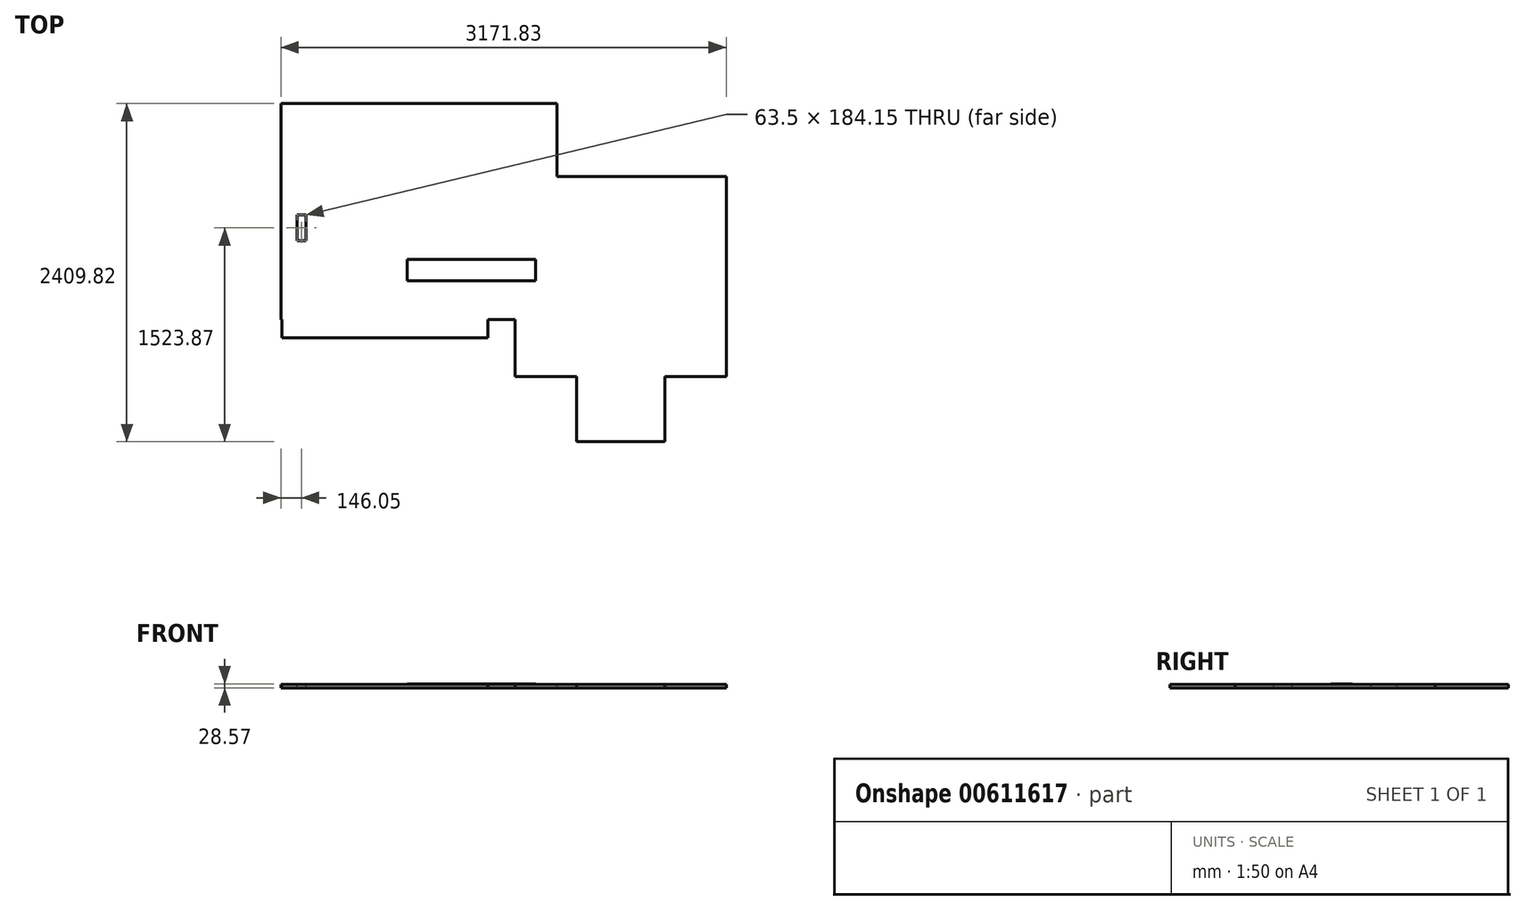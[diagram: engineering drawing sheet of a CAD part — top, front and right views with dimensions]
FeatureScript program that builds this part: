
annotation { "Feature Type Name" : "Feature", "Feature Type Description" : "" }
export const myFeature = defineFeature(function(context is Context, id is Id, definition is map)
    precondition{}
    {
        {
            var Q0;
            Q0=qCreatedBy(makeId("Top.planeOp"),FACE);
            var sketch = newSketch(context, id + "F0", { "sketchPlane" : qUnion([Q0])});
            skLineSegment(sketch, "E0", {"start": v(-1397, 266.7) * mm, "end": v(-1397, -1273.3) * mm});
            skLineSegment(sketch, "E1", {"start": v(-1397, 266.7) * mm, "end": v(568.33, 266.7) * mm});
            skLineSegment(sketch, "E2", {"start": v(1774.83, -254) * mm, "end": v(1774.83, -1679.58) * mm});
            skLineSegment(sketch, "E3", {"start": v(708.15, -2143.12) * mm, "end": v(1336.67, -2143.12) * mm});
            skLineSegment(sketch, "E4", {"start": v(1774.83, -254) * mm, "end": v(568.33, -254) * mm});
            skLineSegment(sketch, "E5", {"start": v(568.33, -254) * mm, "end": v(568.33, 266.7) * mm});
            skLineSegment(sketch, "E6", {"start": v(-1390.65, -1403.48) * mm, "end": v(76.2, -1403.48) * mm});
            skLineSegment(sketch, "E7", {"start": v(76.2, -1403.48) * mm, "end": v(76.2, -1273.17) * mm});
            skLineSegment(sketch, "E8", {"start": v(76.2, -1273.17) * mm, "end": v(270, -1273.17) * mm});
            skLineSegment(sketch, "E9", {"start": v(270, -1273.17) * mm, "end": v(270, -1679.57) * mm});
            skLineSegment(sketch, "E10", {"start": v(270, -1679.57) * mm, "end": v(708.15, -1679.57) * mm});
            skLineSegment(sketch, "E11", {"start": v(708.15, -1679.57) * mm, "end": v(708.15, -2143.12) * mm});
            skLineSegment(sketch, "E12", {"start": v(1774.83, -1679.57) * mm, "end": v(1336.67, -1679.57) * mm});
            skLineSegment(sketch, "E13", {"start": v(1336.67, -1679.57) * mm, "end": v(1336.67, -2143.12) * mm});
            skLineSegment(sketch, "E14", {"start": v(-1397, -1273.3) * mm, "end": v(-1390.65, -1273.3) * mm});
            skLineSegment(sketch, "E15", {"start": v(-1390.65, -1273.3) * mm, "end": v(-1390.65, -1403.48) * mm});
            skLineSegment(sketch, "E16", {"start": v(-1282.7, -711.33) * mm, "end": v(-1219.2, -711.33) * mm});
            skLineSegment(sketch, "E17", {"start": v(-1219.2, -711.33) * mm, "end": v(-1219.2, -527.18) * mm});
            skLineSegment(sketch, "E18", {"start": v(-1219.2, -527.18) * mm, "end": v(-1282.7, -527.18) * mm});
            skLineSegment(sketch, "E19", {"start": v(-1282.7, -527.18) * mm, "end": v(-1282.7, -711.33) * mm});
            skSolve(sketch);
        }
        {
            var Q0;
            Q0 = qSketchRegion(id + "F0", true);
            extrude(context, id + "F1", {"entities" : qUnion([Q0]), "oppositeDirection" : true, "depth" : 25.4 * mm, "offsetDistance" : 25.4 * mm});
        }
        {
            var Q0;
            Q0=makeQuery(id+"F0.imprint","IMPRINT",FACE,{"disambiguationData":[TD([[makeQuery(id+"F0.imprint","IMPRINT",EDGE,{"derivedFrom":sQuery(id+"F0.wireOp",EDGE,"E0")}),1.0]])]});
            var sketch = newSketch(context, id + "F2", { "sketchPlane" : qUnion([Q0])});
            skLineSegment(sketch, "E20.bottom", {"start": v(-497.93, -843.94) * mm, "end": v(416.47, -843.94) * mm});
            skLineSegment(sketch, "E20.top", {"start": v(-497.93, -996.34) * mm, "end": v(416.47, -996.34) * mm});
            skLineSegment(sketch, "E20.left", {"start": v(-497.93, -843.94) * mm, "end": v(-497.93, -996.34) * mm});
            skLineSegment(sketch, "E20.right", {"start": v(416.47, -843.94) * mm, "end": v(416.47, -996.34) * mm});
            skSolve(sketch);
        }
        {
            var Q0;
            Q0 = qSketchRegion(id + "F2", true);
            extrude(context, id + "F3", {"entities" : qUnion([Q0]), "depth" : 3.17 * mm, "offsetDistance" : 25.4 * mm});
        }
    });
